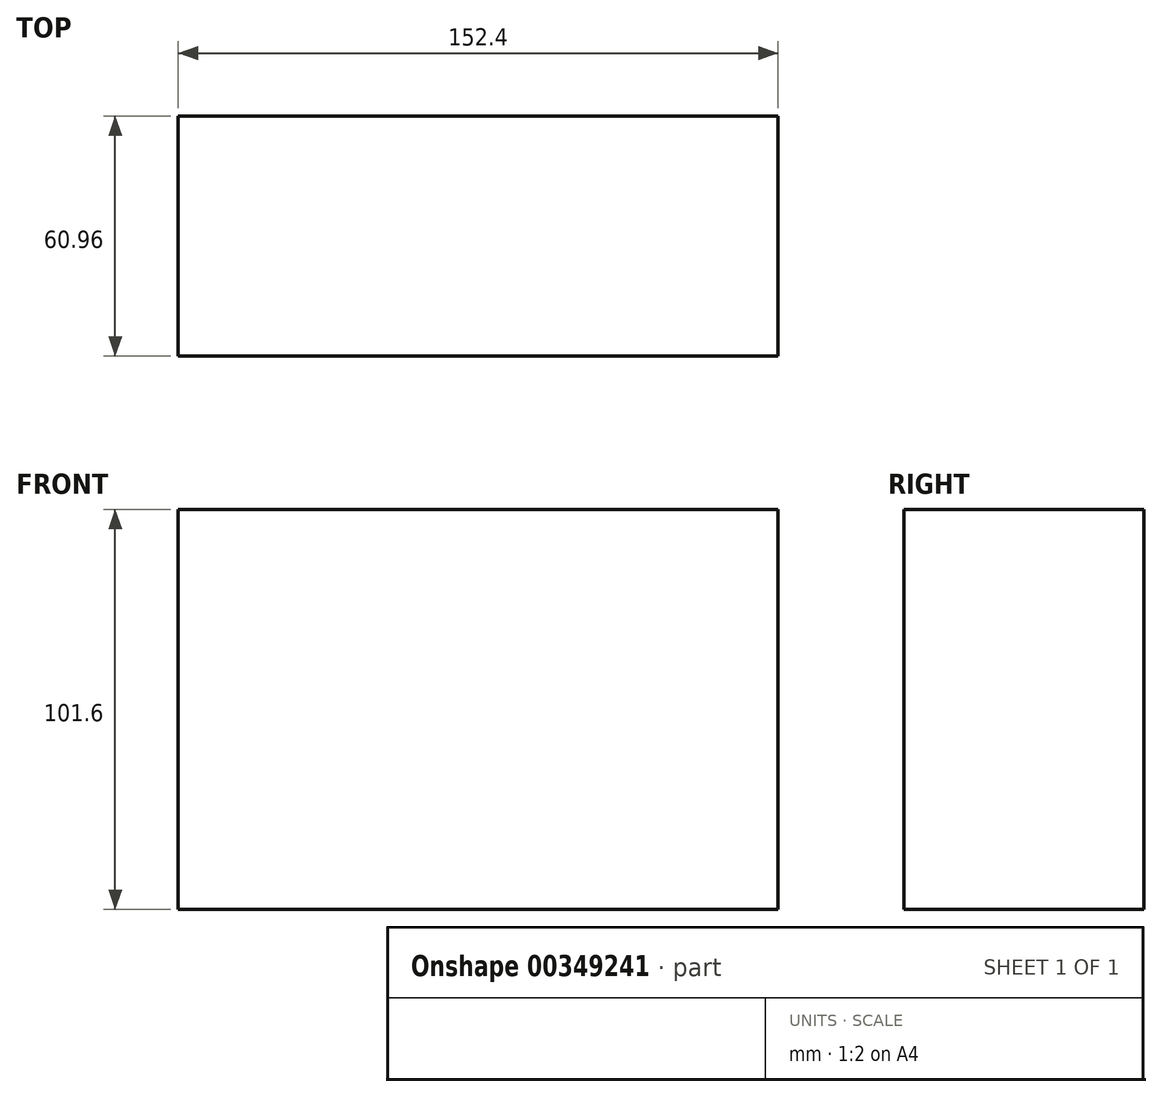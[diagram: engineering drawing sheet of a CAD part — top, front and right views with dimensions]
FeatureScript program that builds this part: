
annotation { "Feature Type Name" : "Feature", "Feature Type Description" : "" }
export const myFeature = defineFeature(function(context is Context, id is Id, definition is map)
    precondition{}
    {
        {
            var Q0;
            Q0=qCreatedBy(makeId("Front.planeOp"),FACE);
            var sketch = newSketch(context, id + "F0", { "sketchPlane" : qUnion([Q0])});
            skLineSegment(sketch, "E0.bottom", {"start": v(-74.48, -35.55) * mm, "end": v(77.92, -35.55) * mm});
            skLineSegment(sketch, "E0.top", {"start": v(-74.48, 66.05) * mm, "end": v(77.92, 66.05) * mm});
            skLineSegment(sketch, "E0.left", {"start": v(-74.48, -35.55) * mm, "end": v(-74.48, 66.05) * mm});
            skLineSegment(sketch, "E0.right", {"start": v(77.92, -35.55) * mm, "end": v(77.92, 66.05) * mm});
            skSolve(sketch);
        }
        {
            var Q0;
            Q0 = qSketchRegion(id + "F0", true);
            extrude(context, id + "F1", {"entities" : qUnion([Q0]), "depth" : 60.96 * mm});
        }
    });
